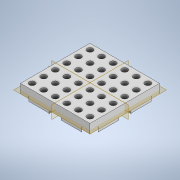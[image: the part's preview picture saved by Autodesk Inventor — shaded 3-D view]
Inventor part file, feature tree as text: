
AUTODESK INVENTOR PART (.ipt)
format: ipt  version: 2022.4 (Build 264492010, 492A)  size: 307,200 bytes
history: native  units: mm
features: extrude x4, sketch x2
ambient origin geometry x8: Origin, YZ Plane, XZ Plane, XY Plane, X Axis, Y Axis, Z Axis, Center Point
bodies: Solid1 (feature_tree)
feature tree (6):
  extrude  "Extrusion1"  Depth=60.0mm
  extrude  "Extrusion2"  Depth=10.0mm
  extrude  "Extrusion3"  Depth=8.0mm
  extrude  "Extrusion4"  Depth=3.0mm
  sketch  "Sketch1"  dims[d0=60.0mm d1=60.0mm]
  sketch  "Sketch3"  dims[d2=10.0mm d3=0.0mm d4=10.0mm d5=8.0mm d6=3.0mm d7=40.0mm d9=360.0deg d11=2.0mm d12=0.0mm d13=4.0mm d14=0.0mm d15=5.0mm d16=5.0mm d17=5.0mm d18=60.0mm d20=10.0mm d21=60.0mm d23=10.0mm d26=5.0mm d27=0.0mm d33=135.0deg d34=5.0mm d35=5.0mm d37=8.0mm d38=3.0mm d39=7.071068mm d45=5.0mm d46=40.0mm d48=360.0deg]
